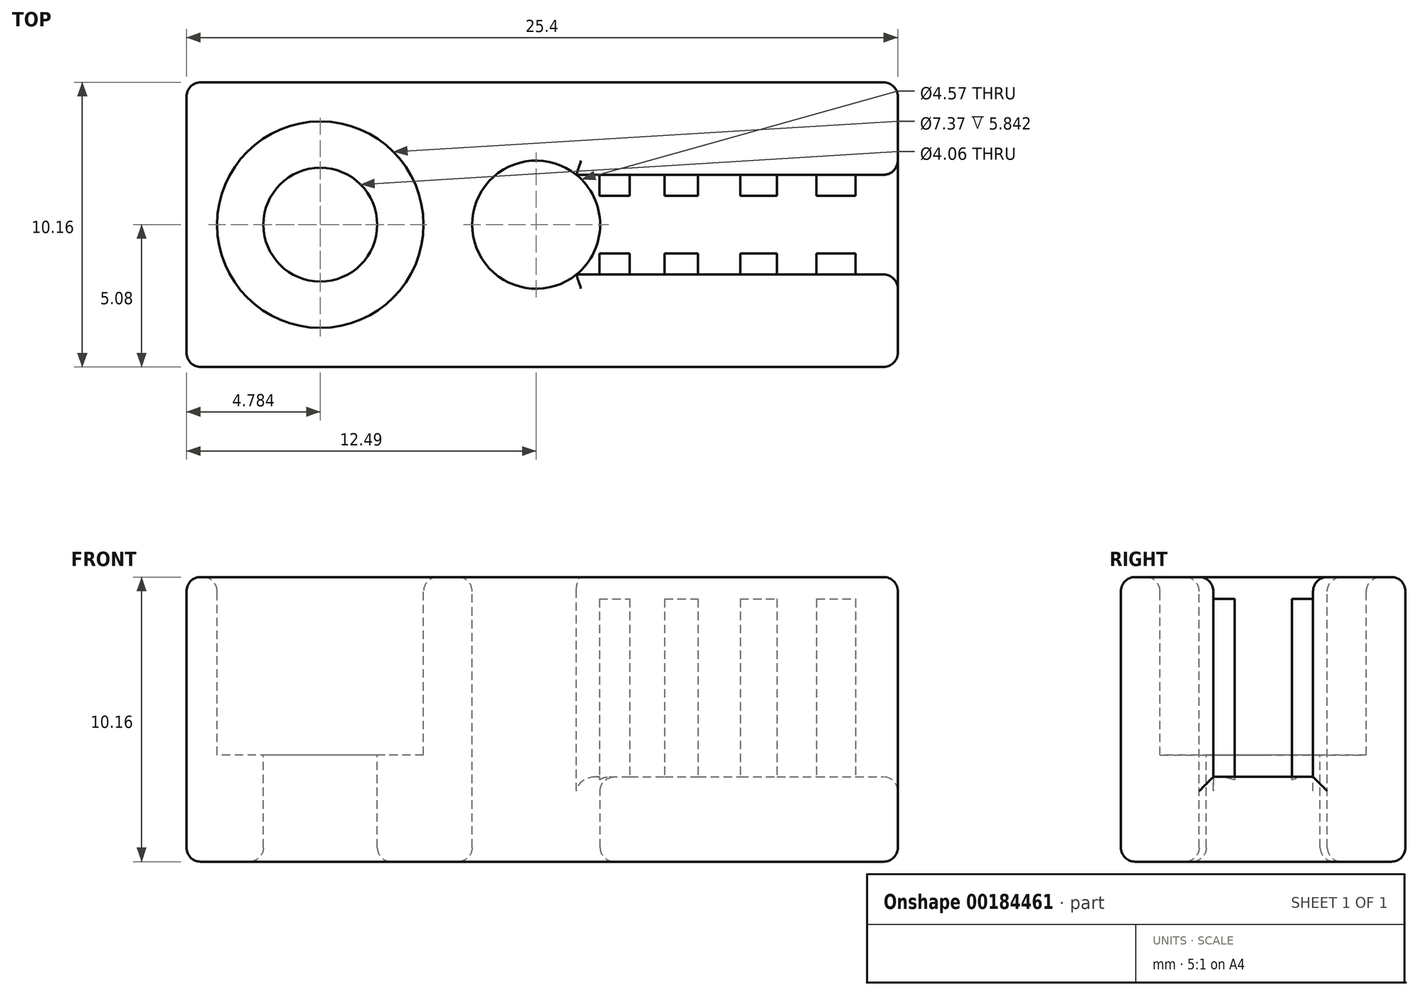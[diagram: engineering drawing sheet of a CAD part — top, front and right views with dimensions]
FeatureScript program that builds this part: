
annotation { "Feature Type Name" : "Feature", "Feature Type Description" : "" }
export const myFeature = defineFeature(function(context is Context, id is Id, definition is map)
    precondition{}
    {
        {
            var Q0;
            Q0=qCreatedBy(makeId("Front.planeOp"),FACE);
            var sketch = newSketch(context, id + "F0", { "sketchPlane" : qUnion([Q0])});
            skLineSegment(sketch, "E0.bottom", {"start": v(-12.49, 5.4) * mm, "end": v(12.91, 5.4) * mm});
            skLineSegment(sketch, "E0.top", {"start": v(-12.49, -4.76) * mm, "end": v(12.91, -4.76) * mm});
            skLineSegment(sketch, "E0.left", {"start": v(-12.49, 5.4) * mm, "end": v(-12.49, -4.76) * mm});
            skLineSegment(sketch, "E0.right", {"start": v(12.91, 5.4) * mm, "end": v(12.91, -4.76) * mm});
            skSolve(sketch);
        }
        {
            var Q0;
            Q0=makeQuery(id+"F0.imprint","IMPRINT",FACE,{"disambiguationData":[TD([[makeQuery(id+"F0.imprint","IMPRINT",EDGE,{"derivedFrom":sQuery(id+"F0.wireOp",EDGE,"E0.bottom")}),-1.0]])]});
            extrude(context, id + "F1", {"entities" : qUnion([Q0]), "depth" : 10.16 * mm});
        }
        {
            var Q0;
            Q0=makeQuery(id+"F1.opExtrude","SWEPT_FACE",FACE,{"disambiguationData":[OSD([sQuery(id+"F0.wireOp",EDGE,"E0.bottom")])]});
            var sketch = newSketch(context, id + "F2", { "sketchPlane" : qUnion([Q0])});
            skCircle(sketch, "E1", {"center": v(-7.7, -5.08) * mm, "radius": 3.69 * mm});
            skPoint(sketch, "E1.centerSnap0", {"position": v(-12.49, -5.08) * mm});
            skSolve(sketch);
        }
        {
            var Q0;
            Q0=makeQuery(id+"F2.imprint","IMPRINT",FACE,{"disambiguationData":[TD([[makeQuery(id+"F2.imprint","IMPRINT",EDGE,{"derivedFrom":sQuery(id+"F2.wireOp",EDGE,"E1")}),1.0]])]});
            extrude(context, id + "F3", {"entities" : qUnion([Q0]), "operationType" : NewBodyOperationType.REMOVE, "oppositeDirection" : true, "depth" : 6.35 * mm});
        }
        {
            var Q0;
            Q0=makeQuery(id+"F1.opExtrude","SWEPT_FACE",FACE,{"disambiguationData":[OSD([sQuery(id+"F0.wireOp",EDGE,"E0.bottom")])]});
            var sketch = newSketch(context, id + "F4", { "sketchPlane" : qUnion([Q0])});
            skCircle(sketch, "E2", {"center": v(0, -5.08) * mm, "radius": 2.29 * mm});
            skPoint(sketch, "E2.centerSnap0", {"position": v(-12.49, -5.08) * mm});
            skSolve(sketch);
        }
        {
            var Q0;
            Q0=makeQuery(id+"F4.imprint","IMPRINT",FACE,{"disambiguationData":[TD([[makeQuery(id+"F4.imprint","IMPRINT",EDGE,{"derivedFrom":sQuery(id+"F4.wireOp",EDGE,"E2")}),1.0]])]});
            extrude(context, id + "F5", {"entities" : qUnion([Q0]), "operationType" : NewBodyOperationType.REMOVE, "endBound" : BoundingType.THROUGH_ALL, "oppositeDirection" : true, "depth" : 25.4 * mm});
        }
        {
            var Q0;
            Q0=makeQuery(id+"F3.boolean.opBoolean","COPY",FACE,{"derivedFrom":makeQuery(id+"F3.opExtrude","CAP_FACE",FACE,{"disambiguationData":[OSD([sQuery(id+"F2.wireOp",EDGE,"E1")])],"isStart":false})});
            var sketch = newSketch(context, id + "F6", { "sketchPlane" : qUnion([Q0])});
            skCircle(sketch, "E3", {"center": v(-7.7, -5.08) * mm, "radius": 2.03 * mm});
            skSolve(sketch);
        }
        {
            var Q0;
            Q0=makeQuery(id+"F6.imprint","IMPRINT",FACE,{"disambiguationData":[TD([[makeQuery(id+"F6.imprint","IMPRINT",EDGE,{"derivedFrom":sQuery(id+"F6.wireOp",EDGE,"E3")}),1.0]])]});
            extrude(context, id + "F7", {"entities" : qUnion([Q0]), "operationType" : NewBodyOperationType.REMOVE, "endBound" : BoundingType.THROUGH_ALL, "oppositeDirection" : true, "depth" : 25.4 * mm});
        }
        {
            var Q0;
            Q0=makeQuery(id+"F1.opExtrude","SWEPT_FACE",FACE,{"disambiguationData":[OSD([sQuery(id+"F0.wireOp",EDGE,"E0.right")])]});
            var sketch = newSketch(context, id + "F8", { "sketchPlane" : qUnion([Q0])});
            skPoint(sketch, "E4.centerSnap0", {"position": v(-5.08, 5.4) * mm});
            skLineSegment(sketch, "E5.bottom", {"start": v(-5.08, 5.4) * mm, "end": v(-6.86, 5.4) * mm});
            skLineSegment(sketch, "E5.top", {"start": v(-5.08, -1.73) * mm, "end": v(-6.86, -1.73) * mm});
            skLineSegment(sketch, "E5.left", {"start": v(-5.08, 5.4) * mm, "end": v(-5.08, -1.73) * mm});
            skLineSegment(sketch, "E5.right", {"start": v(-6.86, 5.4) * mm, "end": v(-6.86, -1.73) * mm});
            skLineSegment(sketch, "E6.MirrorCS", {"start": v(-3.3, 5.4) * mm, "end": v(-3.3, -1.73) * mm});
            skLineSegment(sketch, "E7.MirrorCS", {"start": v(-5.08, -1.73) * mm, "end": v(-3.3, -1.73) * mm});
            skSolve(sketch);
        }
        {
            var Q0;
            Q0 = qSketchRegion(id + "F8", true);
            var Q1;
            {var subQ0=sQuery(id+"F8.wireOp",EDGE,"E5.left");Q1=makeQuery(id+"F8.imprint","IMPRINT",FACE,{"disambiguationData":[TD([[makeQuery(id+"F8.imprint","IMPRINT",EDGE,{"derivedFrom":subQ0}),1.0]])]});}
            extrude(context, id + "F9", {"entities" : qUnion([Q0, Q1]), "operationType" : NewBodyOperationType.REMOVE, "oppositeDirection" : true, "depth" : 12.7 * mm});
        }
        {
            var Q0;
            Q0=makeQuery(id+"F9.boolean.opBoolean","COPY",FACE,{"derivedFrom":makeQuery(id+"F9.opExtrude","SWEPT_FACE",FACE,{"disambiguationData":[OSD([sQuery(id+"F8.wireOp",EDGE,"E5.top"),sQuery(id+"F8.wireOp",EDGE,"E7.MirrorCS")])]})});
            var sketch = newSketch(context, id + "F10", { "sketchPlane" : qUnion([Q0])});
            skLineSegment(sketch, "E8", {"start": v(2.29, -5.08) * mm, "end": v(12.91, -5.08) * mm});
            skLineSegment(sketch, "E9.bottom", {"start": v(2.26, -3.3) * mm, "end": v(3.35, -3.3) * mm});
            skLineSegment(sketch, "E9.top", {"start": v(2.26, -4.06) * mm, "end": v(3.35, -4.06) * mm});
            skLineSegment(sketch, "E9.left", {"start": v(2.26, -3.3) * mm, "end": v(2.26, -4.06) * mm});
            skLineSegment(sketch, "E9.right", {"start": v(3.35, -3.3) * mm, "end": v(3.35, -4.06) * mm});
            skLineSegment(sketch, "E10.bottom", {"start": v(4.59, -3.3) * mm, "end": v(5.77, -3.3) * mm});
            skLineSegment(sketch, "E10.top", {"start": v(4.59, -4.06) * mm, "end": v(5.77, -4.06) * mm});
            skLineSegment(sketch, "E10.left", {"start": v(4.59, -3.3) * mm, "end": v(4.59, -4.06) * mm});
            skLineSegment(sketch, "E10.right", {"start": v(5.77, -3.3) * mm, "end": v(5.77, -4.06) * mm});
            skLineSegment(sketch, "E11.bottom", {"start": v(7.29, -3.3) * mm, "end": v(8.6, -3.3) * mm});
            skLineSegment(sketch, "E11.top", {"start": v(7.29, -4.06) * mm, "end": v(8.6, -4.06) * mm});
            skLineSegment(sketch, "E11.left", {"start": v(7.29, -3.3) * mm, "end": v(7.29, -4.06) * mm});
            skLineSegment(sketch, "E11.right", {"start": v(8.6, -3.3) * mm, "end": v(8.6, -4.06) * mm});
            skLineSegment(sketch, "E12.bottom", {"start": v(10.01, -3.3) * mm, "end": v(11.4, -3.3) * mm});
            skLineSegment(sketch, "E12.top", {"start": v(10.01, -4.06) * mm, "end": v(11.4, -4.06) * mm});
            skLineSegment(sketch, "E12.left", {"start": v(10.01, -3.3) * mm, "end": v(10.01, -4.06) * mm});
            skLineSegment(sketch, "E12.right", {"start": v(11.4, -3.3) * mm, "end": v(11.4, -4.06) * mm});
            skLineSegment(sketch, "E13.MirrorCS", {"start": v(2.26, -6.86) * mm, "end": v(2.26, -6.1) * mm});
            skLineSegment(sketch, "E14.MirrorCS", {"start": v(2.26, -6.1) * mm, "end": v(3.35, -6.1) * mm});
            skLineSegment(sketch, "E15.MirrorCS", {"start": v(3.35, -6.86) * mm, "end": v(3.35, -6.1) * mm});
            skLineSegment(sketch, "E16.MirrorCS", {"start": v(4.59, -6.1) * mm, "end": v(5.77, -6.1) * mm});
            skLineSegment(sketch, "E17.MirrorCS", {"start": v(4.59, -6.86) * mm, "end": v(4.59, -6.1) * mm});
            skLineSegment(sketch, "E18.MirrorCS", {"start": v(5.77, -6.86) * mm, "end": v(5.77, -6.1) * mm});
            skLineSegment(sketch, "E19.MirrorCS", {"start": v(7.29, -6.86) * mm, "end": v(7.29, -6.1) * mm});
            skLineSegment(sketch, "E20.MirrorCS", {"start": v(7.29, -6.1) * mm, "end": v(8.6, -6.1) * mm});
            skLineSegment(sketch, "E21.MirrorCS", {"start": v(8.6, -6.86) * mm, "end": v(8.6, -6.1) * mm});
            skLineSegment(sketch, "E22.MirrorCS", {"start": v(10.01, -6.86) * mm, "end": v(10.01, -6.1) * mm});
            skLineSegment(sketch, "E23.MirrorCS", {"start": v(10.01, -6.1) * mm, "end": v(11.4, -6.1) * mm});
            skLineSegment(sketch, "E24.MirrorCS", {"start": v(11.4, -6.86) * mm, "end": v(11.4, -6.1) * mm});
            skSolve(sketch);
        }
        {
            var Q0;
            Q0=makeQuery(id+"F10.imprint","IMPRINT",FACE,{"disambiguationData":[TD([[makeQuery(id+"F10.imprint","IMPRINT",EDGE,{"derivedFrom":sQuery(id+"F10.wireOp",EDGE,"E9.bottom")}),-1.0]])]});
            var Q1;
            Q1=makeQuery(id+"F10.imprint","IMPRINT",FACE,{"disambiguationData":[TD([[makeQuery(id+"F10.imprint","IMPRINT",EDGE,{"derivedFrom":sQuery(id+"F10.wireOp",EDGE,"E10.bottom")}),-1.0]])]});
            var Q2;
            Q2=makeQuery(id+"F10.imprint","IMPRINT",FACE,{"disambiguationData":[TD([[makeQuery(id+"F10.imprint","IMPRINT",EDGE,{"derivedFrom":sQuery(id+"F10.wireOp",EDGE,"E11.bottom")}),-1.0]])]});
            var Q3;
            Q3=makeQuery(id+"F10.imprint","IMPRINT",FACE,{"disambiguationData":[TD([[makeQuery(id+"F10.imprint","IMPRINT",EDGE,{"derivedFrom":sQuery(id+"F10.wireOp",EDGE,"E12.bottom")}),-1.0]])]});
            var Q4;
            {var subQ0=sQuery(id+"F10.wireOp",EDGE,"E13.MirrorCS");Q4=makeQuery(id+"F10.imprint","IMPRINT",FACE,{"disambiguationData":[TD([[makeQuery(id+"F10.imprint","IMPRINT",EDGE,{"derivedFrom":subQ0}),-1.0]])]});}
            var Q5;
            Q5=makeQuery(id+"F10.imprint","IMPRINT",FACE,{"disambiguationData":[TD([[makeQuery(id+"F10.imprint","IMPRINT",EDGE,{"derivedFrom":sQuery(id+"F10.wireOp",EDGE,"E16.MirrorCS")}),-1.0]])]});
            var Q6;
            {var subQ0=sQuery(id+"F10.wireOp",EDGE,"E19.MirrorCS");Q6=makeQuery(id+"F10.imprint","IMPRINT",FACE,{"disambiguationData":[TD([[makeQuery(id+"F10.imprint","IMPRINT",EDGE,{"derivedFrom":subQ0}),-1.0]])]});}
            var Q7;
            {var subQ0=sQuery(id+"F10.wireOp",EDGE,"E22.MirrorCS");Q7=makeQuery(id+"F10.imprint","IMPRINT",FACE,{"disambiguationData":[TD([[makeQuery(id+"F10.imprint","IMPRINT",EDGE,{"derivedFrom":subQ0}),-1.0]])]});}
            extrude(context, id + "F11", {"entities" : qUnion([Q0, Q1, Q2, Q3, Q4, Q5, Q6, Q7]), "operationType" : NewBodyOperationType.ADD, "depth" : 6.35 * mm});
        }
        {
            var Q0;
            Q0=makeQuery(id+"F1.opExtrude","SWEPT_FACE",FACE,{"disambiguationData":[OSD([sQuery(id+"F0.wireOp",EDGE,"E0.right")])]});
            var Q1;
            Q1=makeQuery(id+"F1.opExtrude","CAP_EDGE",EDGE,{"disambiguationData":[OSD([sQuery(id+"F0.wireOp",EDGE,"E0.bottom")])],"isStart":true});
            var Q2;
            Q2=makeQuery(id+"F1.opExtrude","CAP_EDGE",EDGE,{"disambiguationData":[OSD([sQuery(id+"F0.wireOp",EDGE,"E0.bottom")])],"isStart":false});
            var Q3;
            Q3=makeQuery(id+"F1.opExtrude","SWEPT_EDGE",EDGE,{"disambiguationData":[OSD([sQuery(id+"F0.wireOp",EDGE,"E0.top"),sQuery(id+"F0.wireOp",EDGE,"E0.left")])]});
            var Q4;
            Q4=makeQuery(id+"F1.opExtrude","CAP_EDGE",EDGE,{"disambiguationData":[OSD([sQuery(id+"F0.wireOp",EDGE,"E0.top")])],"isStart":true});
            var Q5;
            Q5=makeQuery(id+"F1.opExtrude","CAP_EDGE",EDGE,{"disambiguationData":[OSD([sQuery(id+"F0.wireOp",EDGE,"E0.left")])],"isStart":true});
            var Q6;
            Q6=makeQuery(id+"F1.opExtrude","CAP_EDGE",EDGE,{"disambiguationData":[OSD([sQuery(id+"F0.wireOp",EDGE,"E0.top")])],"isStart":false});
            var Q7;
            Q7=makeQuery(id+"F1.opExtrude","CAP_EDGE",EDGE,{"disambiguationData":[OSD([sQuery(id+"F0.wireOp",EDGE,"E0.left")])],"isStart":false});
            var Q8;
            Q8=makeQuery(id+"F1.opExtrude","SWEPT_EDGE",EDGE,{"disambiguationData":[OSD([sQuery(id+"F0.wireOp",EDGE,"E0.bottom"),sQuery(id+"F0.wireOp",EDGE,"E0.left")])]});
            var Q9;
            Q9=makeQuery(id+"F3.boolean.opBoolean","COPY",EDGE,{"derivedFrom":makeQuery(id+"F3.opExtrude","CAP_EDGE",EDGE,{"disambiguationData":[OSD([sQuery(id+"F2.wireOp",EDGE,"E1")])],"isStart":true})});
            var Q10;
            Q10=makeQuery(id+"F5.boolean.opBoolean","COPY",EDGE,{"derivedFrom":makeQuery(id+"F5.opExtrude","CAP_EDGE",EDGE,{"disambiguationData":[OSD([sQuery(id+"F4.wireOp",EDGE,"E2")])],"isStart":true})});
            var Q11;
            Q11=makeQuery(id+"F1.opExtrude","SWEPT_FACE",FACE,{"disambiguationData":[OSD([sQuery(id+"F0.wireOp",EDGE,"E0.bottom")])]});
            var Q12;
            Q12=makeQuery(id+"F7.boolean.opBoolean","COPY",EDGE,{"derivedFrom":makeQuery(id+"F7.opExtrude","CAP_EDGE",EDGE,{"disambiguationData":[OSD([sQuery(id+"F6.wireOp",EDGE,"E3")])],"isStart":true})});
            var Q13;
            Q13=makeQuery(id+"F9.boolean.opBoolean","INTERSECT",EDGE,{"derivedFrom":[makeQuery(id+"F5.boolean.opBoolean","COPY",FACE,{"derivedFrom":makeQuery(id+"F5.opExtrude","SWEPT_FACE",FACE,{"disambiguationData":[OSD([sQuery(id+"F4.wireOp",EDGE,"E2")])]})}),makeQuery(id+"F9.opExtrude","SWEPT_FACE",FACE,{"disambiguationData":[OSD([sQuery(id+"F8.wireOp",EDGE,"E5.top"),sQuery(id+"F8.wireOp",EDGE,"E7.MirrorCS")])]})]});
            var Q14;
            Q14=makeQuery(id+"F5.boolean.opBoolean","INTERSECT",EDGE,{"derivedFrom":[makeQuery(id+"F1.opExtrude","SWEPT_FACE",FACE,{"disambiguationData":[OSD([sQuery(id+"F0.wireOp",EDGE,"E0.top")])]}),makeQuery(id+"F5.opExtrude","SWEPT_FACE",FACE,{"disambiguationData":[OSD([sQuery(id+"F4.wireOp",EDGE,"E2")])]})]});
            var Q15;
            Q15=makeQuery(id+"F7.boolean.opBoolean","INTERSECT",EDGE,{"derivedFrom":[makeQuery(id+"F1.opExtrude","SWEPT_FACE",FACE,{"disambiguationData":[OSD([sQuery(id+"F0.wireOp",EDGE,"E0.top")])]}),makeQuery(id+"F7.opExtrude","SWEPT_FACE",FACE,{"disambiguationData":[OSD([sQuery(id+"F6.wireOp",EDGE,"E3")])]})]});
            fillet(context, id + "F12", {"entities" : qUnion([Q0, Q1, Q2, Q3, Q4, Q5, Q6, Q7, Q8, Q9, Q10, Q11, Q12, Q13, Q14, Q15]), "radius" : 0.5 * mm, "tangentPropagation" : true, "allowEdgeOverflow" : false});
        }
    });
